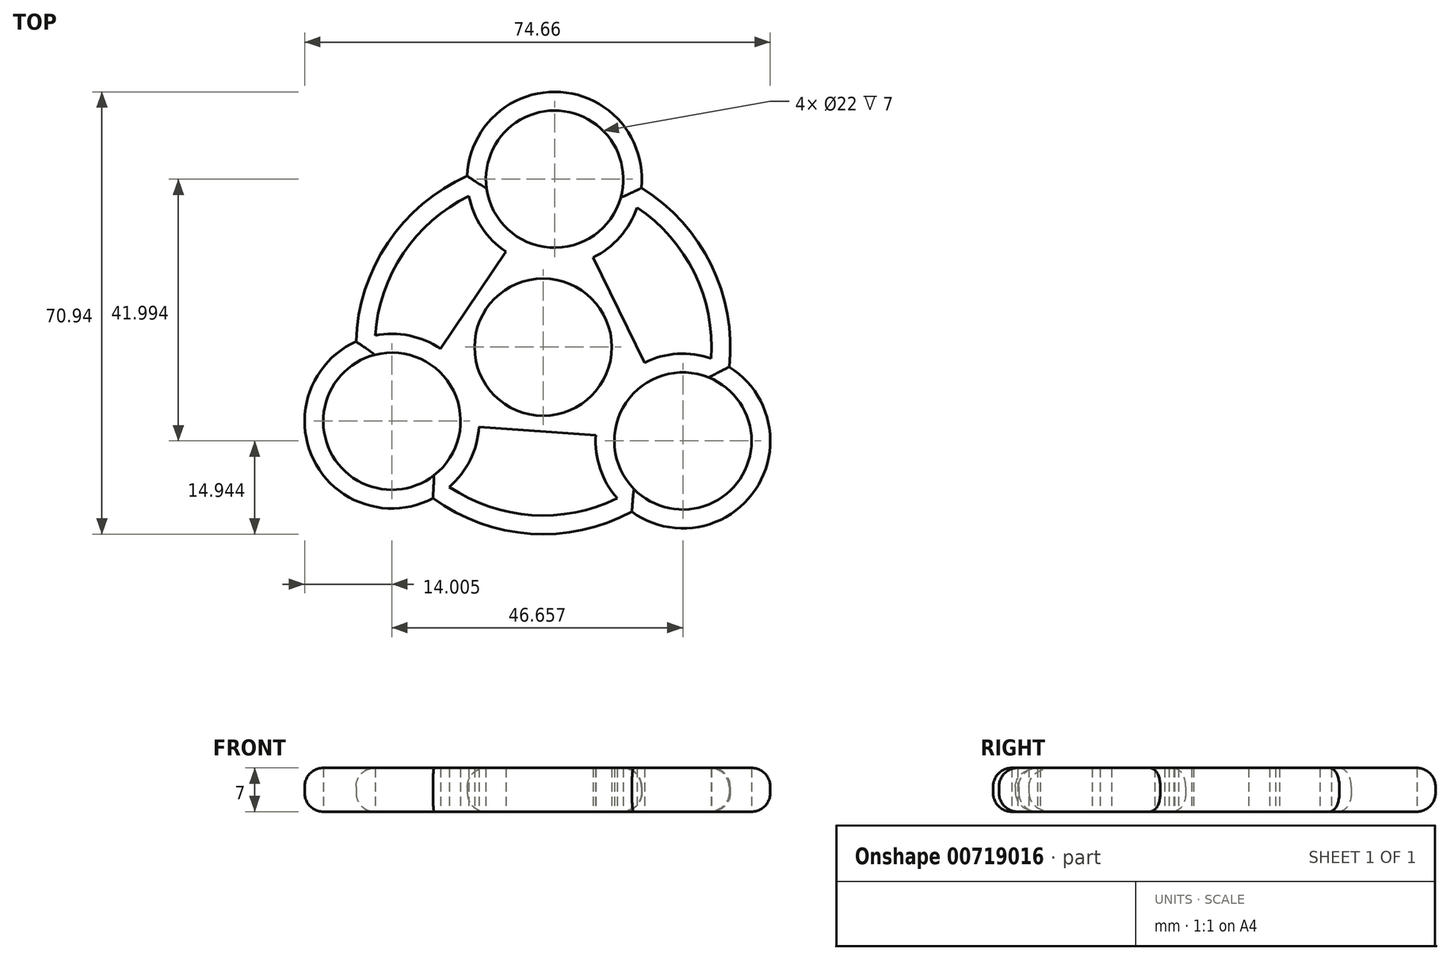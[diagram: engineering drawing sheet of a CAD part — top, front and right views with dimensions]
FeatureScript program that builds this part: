
annotation { "Feature Type Name" : "Feature", "Feature Type Description" : "" }
export const myFeature = defineFeature(function(context is Context, id is Id, definition is map)
    precondition{}
    {
        {
            var Q0;
            Q0=qCreatedBy(makeId("Top.planeOp"),FACE);
            var sketch = newSketch(context, id + "F0", { "sketchPlane" : qUnion([Q0])});
            skCircle(sketch, "E0", {"center": v(0, 0) * mm, "radius": 11 * mm});
            skCircle(sketch, "E1.cCircle", {"center": v(0, 0) * mm, "radius": 27 * mm, "construction": true});
            skLineSegment(sketch, "E1.0", {"start": v(22.41, -15.06) * mm, "end": v(-24.25, -11.88) * mm});
            skLineSegment(sketch, "E1.1", {"start": v(-24.25, -11.88) * mm, "end": v(1.83, 26.94) * mm});
            skLineSegment(sketch, "E1.2", {"start": v(1.83, 26.94) * mm, "end": v(22.41, -15.06) * mm});
            skCircle(sketch, "E2", {"center": v(-24.25, -11.88) * mm, "radius": 11 * mm});
            skCircle(sketch, "E3", {"center": v(1.83, 26.94) * mm, "radius": 11 * mm});
            skCircle(sketch, "E4", {"center": v(22.41, -15.06) * mm, "radius": 11 * mm});
            skCircle(sketch, "E5", {"center": v(-24.25, -11.88) * mm, "radius": 14 * mm});
            skCircle(sketch, "E6", {"center": v(22.41, -15.06) * mm, "radius": 14 * mm});
            skCircle(sketch, "E7", {"center": v(0, 0) * mm, "radius": 15 * mm});
            skCircle(sketch, "E8", {"center": v(1.83, 26.94) * mm, "radius": 14 * mm});
            skCircle(sketch, "E9", {"center": v(0, 0) * mm, "radius": 30 * mm});
            skCircle(sketch, "E10", {"center": v(0, 0) * mm, "radius": 27 * mm});
            skSolve(sketch);
        }
        {
            var Q0;
            {var subQ0=sQuery(id+"F0.wireOp",EDGE,"E9");var subQ1=sQuery(id+"F0.wireOp",EDGE,"E5");var subQ2=makeQuery(id+"F0.imprint","INTERSECT",VERTEX,{"disambiguationData":[OD(1.0)],"derivedFrom":[subQ1,subQ0]});Q0=makeQuery(id+"F0.imprint","IMPRINT",FACE,{"disambiguationData":[TD([[makeQuery(id+"F0.imprint","IMPRINT",EDGE,{"disambiguationData":[TD([[subQ2,-1.0]])],"derivedFrom":subQ1}),-1.0]])]});}
            var Q1;
            {var subQ0=sQuery(id+"F0.wireOp",EDGE,"E9");var subQ1=sQuery(id+"F0.wireOp",EDGE,"E4");var subQ2=makeQuery(id+"F0.imprint","INTERSECT",VERTEX,{"disambiguationData":[OD(0.0)],"derivedFrom":[subQ1,subQ0]});Q1=makeQuery(id+"F0.imprint","IMPRINT",FACE,{"disambiguationData":[TD([[makeQuery(id+"F0.imprint","IMPRINT",EDGE,{"disambiguationData":[TD([[subQ2,1.0]])],"derivedFrom":subQ1}),-1.0]])]});}
            var Q2;
            {var subQ0=sQuery(id+"F0.wireOp",EDGE,"E10");var subQ1=sQuery(id+"F0.wireOp",EDGE,"E4");var subQ2=makeQuery(id+"F0.imprint","INTERSECT",VERTEX,{"disambiguationData":[OD(1.0)],"derivedFrom":[subQ1,subQ0]});Q2=makeQuery(id+"F0.imprint","IMPRINT",FACE,{"disambiguationData":[TD([[makeQuery(id+"F0.imprint","IMPRINT",EDGE,{"disambiguationData":[TD([[subQ2,-1.0]])],"derivedFrom":subQ1}),-1.0]])]});}
            var Q3;
            {var subQ0=sQuery(id+"F0.wireOp",EDGE,"E4");var subQ1=sQuery(id+"F0.wireOp",EDGE,"E1.0");var subQ2=makeQuery(id+"F0.imprint","INTERSECT",VERTEX,{"derivedFrom":[subQ1,subQ0]});Q3=makeQuery(id+"F0.imprint","IMPRINT",FACE,{"disambiguationData":[TD([[makeQuery(id+"F0.imprint","IMPRINT",EDGE,{"disambiguationData":[TD([[subQ2,-1.0]])],"derivedFrom":subQ1}),1.0]])]});}
            var Q4;
            {var subQ0=sQuery(id+"F0.wireOp",EDGE,"E10");var subQ1=sQuery(id+"F0.wireOp",EDGE,"E4");var subQ2=makeQuery(id+"F0.imprint","INTERSECT",VERTEX,{"disambiguationData":[OD(0.0)],"derivedFrom":[subQ1,subQ0]});Q4=makeQuery(id+"F0.imprint","IMPRINT",FACE,{"disambiguationData":[TD([[makeQuery(id+"F0.imprint","IMPRINT",EDGE,{"disambiguationData":[TD([[subQ2,1.0]])],"derivedFrom":subQ1}),-1.0]])]});}
            var Q5;
            {var subQ0=sQuery(id+"F0.wireOp",EDGE,"E9");var subQ1=sQuery(id+"F0.wireOp",EDGE,"E6");var subQ2=makeQuery(id+"F0.imprint","INTERSECT",VERTEX,{"disambiguationData":[OD(0.0)],"derivedFrom":[subQ1,subQ0]});Q5=makeQuery(id+"F0.imprint","IMPRINT",FACE,{"disambiguationData":[TD([[makeQuery(id+"F0.imprint","IMPRINT",EDGE,{"disambiguationData":[TD([[subQ2,-1.0]])],"derivedFrom":subQ1}),-1.0]])]});}
            var Q6;
            {var subQ0=sQuery(id+"F0.wireOp",EDGE,"E9");var subQ1=sQuery(id+"F0.wireOp",EDGE,"E3");var subQ2=makeQuery(id+"F0.imprint","INTERSECT",VERTEX,{"disambiguationData":[OD(0.0)],"derivedFrom":[subQ1,subQ0]});Q6=makeQuery(id+"F0.imprint","IMPRINT",FACE,{"disambiguationData":[TD([[makeQuery(id+"F0.imprint","IMPRINT",EDGE,{"disambiguationData":[TD([[subQ2,1.0]])],"derivedFrom":subQ1}),-1.0]])]});}
            var Q7;
            {var subQ0=sQuery(id+"F0.wireOp",EDGE,"E9");var subQ1=sQuery(id+"F0.wireOp",EDGE,"E2");var subQ2=makeQuery(id+"F0.imprint","INTERSECT",VERTEX,{"disambiguationData":[OD(0.0)],"derivedFrom":[subQ1,subQ0]});Q7=makeQuery(id+"F0.imprint","IMPRINT",FACE,{"disambiguationData":[TD([[makeQuery(id+"F0.imprint","IMPRINT",EDGE,{"disambiguationData":[TD([[subQ2,-1.0]])],"derivedFrom":subQ1}),-1.0]])]});}
            var Q8;
            {var subQ0=sQuery(id+"F0.wireOp",EDGE,"E9");var subQ1=sQuery(id+"F0.wireOp",EDGE,"E2");var subQ2=makeQuery(id+"F0.imprint","INTERSECT",VERTEX,{"disambiguationData":[OD(1.0)],"derivedFrom":[subQ1,subQ0]});Q8=makeQuery(id+"F0.imprint","IMPRINT",FACE,{"disambiguationData":[TD([[makeQuery(id+"F0.imprint","IMPRINT",EDGE,{"disambiguationData":[TD([[subQ2,-1.0]])],"derivedFrom":subQ1}),-1.0]])]});}
            var Q9;
            {var subQ0=sQuery(id+"F0.wireOp",EDGE,"E9");var subQ1=sQuery(id+"F0.wireOp",EDGE,"E5");var subQ2=makeQuery(id+"F0.imprint","INTERSECT",VERTEX,{"disambiguationData":[OD(0.0)],"derivedFrom":[subQ1,subQ0]});Q9=makeQuery(id+"F0.imprint","IMPRINT",FACE,{"disambiguationData":[TD([[makeQuery(id+"F0.imprint","IMPRINT",EDGE,{"disambiguationData":[TD([[subQ2,1.0]])],"derivedFrom":subQ1}),-1.0]])]});}
            var Q10;
            {var subQ0=sQuery(id+"F0.wireOp",EDGE,"E10");var subQ1=sQuery(id+"F0.wireOp",EDGE,"E2");var subQ2=makeQuery(id+"F0.imprint","INTERSECT",VERTEX,{"disambiguationData":[OD(0.0)],"derivedFrom":[subQ1,subQ0]});Q10=makeQuery(id+"F0.imprint","IMPRINT",FACE,{"disambiguationData":[TD([[makeQuery(id+"F0.imprint","IMPRINT",EDGE,{"disambiguationData":[TD([[subQ2,-1.0]])],"derivedFrom":subQ1}),-1.0]])]});}
            var Q11;
            {var subQ0=sQuery(id+"F0.wireOp",EDGE,"E5");var subQ1=sQuery(id+"F0.wireOp",EDGE,"E1.0");var subQ2=makeQuery(id+"F0.imprint","INTERSECT",VERTEX,{"derivedFrom":[subQ1,subQ0]});Q11=makeQuery(id+"F0.imprint","IMPRINT",FACE,{"disambiguationData":[TD([[makeQuery(id+"F0.imprint","IMPRINT",EDGE,{"disambiguationData":[TD([[subQ2,-1.0]])],"derivedFrom":subQ1}),1.0]])]});}
            var Q12;
            {var subQ0=sQuery(id+"F0.wireOp",EDGE,"E2");var subQ1=sQuery(id+"F0.wireOp",EDGE,"E1.1");var subQ2=makeQuery(id+"F0.imprint","INTERSECT",VERTEX,{"derivedFrom":[subQ1,subQ0]});Q12=makeQuery(id+"F0.imprint","IMPRINT",FACE,{"disambiguationData":[TD([[makeQuery(id+"F0.imprint","IMPRINT",EDGE,{"disambiguationData":[TD([[subQ2,-1.0]])],"derivedFrom":subQ1}),1.0]])]});}
            var Q13;
            {var subQ0=sQuery(id+"F0.wireOp",EDGE,"E3");var subQ1=sQuery(id+"F0.wireOp",EDGE,"E1.2");var subQ2=makeQuery(id+"F0.imprint","INTERSECT",VERTEX,{"derivedFrom":[subQ1,subQ0]});Q13=makeQuery(id+"F0.imprint","IMPRINT",FACE,{"disambiguationData":[TD([[makeQuery(id+"F0.imprint","IMPRINT",EDGE,{"disambiguationData":[TD([[subQ2,-1.0]])],"derivedFrom":subQ1}),1.0]])]});}
            var Q14;
            {var subQ0=sQuery(id+"F0.wireOp",EDGE,"E6");var subQ1=sQuery(id+"F0.wireOp",EDGE,"E1.2");var subQ2=makeQuery(id+"F0.imprint","INTERSECT",VERTEX,{"derivedFrom":[subQ1,subQ0]});Q14=makeQuery(id+"F0.imprint","IMPRINT",FACE,{"disambiguationData":[TD([[makeQuery(id+"F0.imprint","IMPRINT",EDGE,{"disambiguationData":[TD([[subQ2,-1.0]])],"derivedFrom":subQ1}),1.0]])]});}
            var Q15;
            {var subQ0=sQuery(id+"F0.wireOp",EDGE,"E9");var subQ1=sQuery(id+"F0.wireOp",EDGE,"E3");var subQ2=makeQuery(id+"F0.imprint","INTERSECT",VERTEX,{"disambiguationData":[OD(1.0)],"derivedFrom":[subQ1,subQ0]});Q15=makeQuery(id+"F0.imprint","IMPRINT",FACE,{"disambiguationData":[TD([[makeQuery(id+"F0.imprint","IMPRINT",EDGE,{"disambiguationData":[TD([[subQ2,1.0]])],"derivedFrom":subQ1}),-1.0]])]});}
            var Q16;
            {var subQ0=sQuery(id+"F0.wireOp",EDGE,"E9");var subQ1=sQuery(id+"F0.wireOp",EDGE,"E3");var subQ2=makeQuery(id+"F0.imprint","INTERSECT",VERTEX,{"disambiguationData":[OD(0.0)],"derivedFrom":[subQ1,subQ0]});Q16=makeQuery(id+"F0.imprint","IMPRINT",FACE,{"disambiguationData":[TD([[makeQuery(id+"F0.imprint","IMPRINT",EDGE,{"disambiguationData":[TD([[subQ2,-1.0]])],"derivedFrom":subQ1}),-1.0]])]});}
            var Q17;
            {var subQ0=sQuery(id+"F0.wireOp",EDGE,"E8");var subQ1=sQuery(id+"F0.wireOp",EDGE,"E1.1");var subQ2=makeQuery(id+"F0.imprint","INTERSECT",VERTEX,{"derivedFrom":[subQ1,subQ0]});Q17=makeQuery(id+"F0.imprint","IMPRINT",FACE,{"disambiguationData":[TD([[makeQuery(id+"F0.imprint","IMPRINT",EDGE,{"disambiguationData":[TD([[subQ2,-1.0]])],"derivedFrom":subQ1}),1.0]])]});}
            var Q18;
            {var subQ0=sQuery(id+"F0.wireOp",EDGE,"E4");var subQ1=sQuery(id+"F0.wireOp",EDGE,"E1.0");var subQ2=makeQuery(id+"F0.imprint","INTERSECT",VERTEX,{"derivedFrom":[subQ1,subQ0]});Q18=makeQuery(id+"F0.imprint","IMPRINT",FACE,{"disambiguationData":[TD([[makeQuery(id+"F0.imprint","IMPRINT",EDGE,{"disambiguationData":[TD([[subQ2,-1.0]])],"derivedFrom":subQ1}),-1.0]])]});}
            var Q19;
            {var subQ1=sQuery(id+"F0.wireOp",EDGE,"E1.0");var subQ5=sQuery(id+"F0.wireOp",EDGE,"E5");var subQ9=makeQuery(id+"F0.imprint","INTERSECT",VERTEX,{"derivedFrom":[subQ1,subQ5]});Q19=makeQuery(id+"F0.imprint","IMPRINT",FACE,{"disambiguationData":[TD([[makeQuery(id+"F0.imprint","IMPRINT",EDGE,{"disambiguationData":[TD([[subQ9,-1.0]])],"derivedFrom":subQ1}),-1.0]])]});}
            var Q20;
            {var subQ1=sQuery(id+"F0.wireOp",EDGE,"E1.1");var subQ5=sQuery(id+"F0.wireOp",EDGE,"E8");var subQ10=makeQuery(id+"F0.imprint","INTERSECT",VERTEX,{"derivedFrom":[subQ1,subQ5]});Q20=makeQuery(id+"F0.imprint","IMPRINT",FACE,{"disambiguationData":[TD([[makeQuery(id+"F0.imprint","IMPRINT",EDGE,{"disambiguationData":[TD([[subQ10,-1.0]])],"derivedFrom":subQ1}),-1.0]])]});}
            var Q21;
            {var subQ0=sQuery(id+"F0.wireOp",EDGE,"E7");var subQ1=sQuery(id+"F0.wireOp",EDGE,"E1.2");var subQ2=makeQuery(id+"F0.imprint","INTERSECT",VERTEX,{"disambiguationData":[OD(1.0)],"derivedFrom":[subQ1,subQ0]});Q21=makeQuery(id+"F0.imprint","IMPRINT",FACE,{"disambiguationData":[TD([[makeQuery(id+"F0.imprint","IMPRINT",EDGE,{"disambiguationData":[TD([[subQ2,-1.0]])],"derivedFrom":subQ1}),-1.0]])]});}
            var Q22;
            {var subQ0=sQuery(id+"F0.wireOp",EDGE,"E6");var subQ1=sQuery(id+"F0.wireOp",EDGE,"E1.0");var subQ2=makeQuery(id+"F0.imprint","INTERSECT",VERTEX,{"derivedFrom":[subQ1,subQ0]});Q22=makeQuery(id+"F0.imprint","IMPRINT",FACE,{"disambiguationData":[TD([[makeQuery(id+"F0.imprint","IMPRINT",EDGE,{"disambiguationData":[TD([[subQ2,-1.0]])],"derivedFrom":subQ1}),-1.0]])]});}
            var Q23;
            {var subQ0=sQuery(id+"F0.wireOp",EDGE,"E7");var subQ1=sQuery(id+"F0.wireOp",EDGE,"E1.0");var subQ2=makeQuery(id+"F0.imprint","INTERSECT",VERTEX,{"disambiguationData":[OD(1.0)],"derivedFrom":[subQ1,subQ0]});Q23=makeQuery(id+"F0.imprint","IMPRINT",FACE,{"disambiguationData":[TD([[makeQuery(id+"F0.imprint","IMPRINT",EDGE,{"disambiguationData":[TD([[subQ2,-1.0]])],"derivedFrom":subQ1}),-1.0]])]});}
            var Q24;
            {var subQ0=sQuery(id+"F0.wireOp",EDGE,"E5");var subQ1=sQuery(id+"F0.wireOp",EDGE,"E1.1");var subQ2=makeQuery(id+"F0.imprint","INTERSECT",VERTEX,{"derivedFrom":[subQ1,subQ0]});Q24=makeQuery(id+"F0.imprint","IMPRINT",FACE,{"disambiguationData":[TD([[makeQuery(id+"F0.imprint","IMPRINT",EDGE,{"disambiguationData":[TD([[subQ2,-1.0]])],"derivedFrom":subQ1}),-1.0]])]});}
            var Q25;
            {var subQ0=sQuery(id+"F0.wireOp",EDGE,"E7");var subQ1=sQuery(id+"F0.wireOp",EDGE,"E1.1");var subQ2=makeQuery(id+"F0.imprint","INTERSECT",VERTEX,{"disambiguationData":[OD(1.0)],"derivedFrom":[subQ1,subQ0]});Q25=makeQuery(id+"F0.imprint","IMPRINT",FACE,{"disambiguationData":[TD([[makeQuery(id+"F0.imprint","IMPRINT",EDGE,{"disambiguationData":[TD([[subQ2,-1.0]])],"derivedFrom":subQ1}),-1.0]])]});}
            var Q26;
            {var subQ0=sQuery(id+"F0.wireOp",EDGE,"E8");var subQ1=sQuery(id+"F0.wireOp",EDGE,"E1.2");var subQ2=makeQuery(id+"F0.imprint","INTERSECT",VERTEX,{"derivedFrom":[subQ1,subQ0]});Q26=makeQuery(id+"F0.imprint","IMPRINT",FACE,{"disambiguationData":[TD([[makeQuery(id+"F0.imprint","IMPRINT",EDGE,{"disambiguationData":[TD([[subQ2,-1.0]])],"derivedFrom":subQ1}),-1.0]])]});}
            var Q27;
            Q27=makeQuery(id+"F0.imprint","IMPRINT",FACE,{"disambiguationData":[TD([[makeQuery(id+"F0.imprint","IMPRINT",EDGE,{"derivedFrom":sQuery(id+"F0.wireOp",EDGE,"E0")}),-1.0]])]});
            var Q28;
            {var subQ0=sQuery(id+"F0.wireOp",EDGE,"E7");var subQ1=sQuery(id+"F0.wireOp",EDGE,"E5");var subQ2=makeQuery(id+"F0.imprint","INTERSECT",VERTEX,{"disambiguationData":[OD(0.0)],"derivedFrom":[subQ1,subQ0]});Q28=makeQuery(id+"F0.imprint","IMPRINT",FACE,{"disambiguationData":[TD([[makeQuery(id+"F0.imprint","IMPRINT",EDGE,{"disambiguationData":[TD([[subQ2,1.0]])],"derivedFrom":subQ1}),1.0]])]});}
            var Q29;
            {var subQ0=sQuery(id+"F0.wireOp",EDGE,"E8");var subQ1=sQuery(id+"F0.wireOp",EDGE,"E7");var subQ2=makeQuery(id+"F0.imprint","INTERSECT",VERTEX,{"disambiguationData":[OD(0.0)],"derivedFrom":[subQ1,subQ0]});Q29=makeQuery(id+"F0.imprint","IMPRINT",FACE,{"disambiguationData":[TD([[makeQuery(id+"F0.imprint","IMPRINT",EDGE,{"disambiguationData":[TD([[subQ2,-1.0]])],"derivedFrom":subQ1}),1.0]])]});}
            var Q30;
            {var subQ0=sQuery(id+"F0.wireOp",EDGE,"E7");var subQ1=sQuery(id+"F0.wireOp",EDGE,"E6");var subQ2=makeQuery(id+"F0.imprint","INTERSECT",VERTEX,{"disambiguationData":[OD(0.0)],"derivedFrom":[subQ1,subQ0]});Q30=makeQuery(id+"F0.imprint","IMPRINT",FACE,{"disambiguationData":[TD([[makeQuery(id+"F0.imprint","IMPRINT",EDGE,{"disambiguationData":[TD([[subQ2,-1.0]])],"derivedFrom":subQ1}),1.0]])]});}
            extrude(context, id + "F1", {"entities" : qUnion([Q0, Q1, Q2, Q3, Q4, Q5, Q6, Q7, Q8, Q9, Q10, Q11, Q12, Q13, Q14, Q15, Q16, Q17, Q18, Q19, Q20, Q21, Q22, Q23, Q24, Q25, Q26, Q27, Q28, Q29, Q30]), "depth" : 7 * mm, "offsetDistance" : 25 * mm});
        }
        {
            var Q0;
            {var subQ0=sQuery(id+"F0.wireOp",EDGE,"E9");Q0=makeQuery(id+"F1.opExtrude","CAP_EDGE",EDGE,{"disambiguationData":[OSD([subQ0]),TDD([makeQuery(id+"F0.imprint","IMPRINT",EDGE,{"disambiguationData":[TD([[makeQuery(id+"F0.imprint","INTERSECT",VERTEX,{"disambiguationData":[OD(1.0)],"derivedFrom":[sQuery(id+"F0.wireOp",EDGE,"E5"),subQ0]}),-1.0]])],"derivedFrom":subQ0})])],"isStart":false});}
            var Q1;
            {var subQ0=sQuery(id+"F0.wireOp",EDGE,"E9");var subQ1=sQuery(id+"F0.wireOp",EDGE,"E6");Q1=makeQuery(id+"F1.opExtrude","CAP_EDGE",EDGE,{"disambiguationData":[OSD([subQ1]),TDD([makeQuery(id+"F0.imprint","IMPRINT",EDGE,{"disambiguationData":[TD([[makeQuery(id+"F0.imprint","INTERSECT",VERTEX,{"disambiguationData":[OD(0.0)],"derivedFrom":[subQ1,subQ0]}),1.0]])],"derivedFrom":subQ1})])],"isStart":false});}
            var Q2;
            {var subQ0=sQuery(id+"F0.wireOp",EDGE,"E9");var subQ1=sQuery(id+"F0.wireOp",EDGE,"E8");Q2=makeQuery(id+"F1.opExtrude","CAP_EDGE",EDGE,{"disambiguationData":[OSD([subQ1]),TDD([makeQuery(id+"F0.imprint","IMPRINT",EDGE,{"disambiguationData":[TD([[makeQuery(id+"F0.imprint","INTERSECT",VERTEX,{"disambiguationData":[OD(0.0)],"derivedFrom":[subQ1,subQ0]}),1.0]])],"derivedFrom":subQ1})])],"isStart":false});}
            var Q3;
            {var subQ0=sQuery(id+"F0.wireOp",EDGE,"E9");Q3=makeQuery(id+"F1.opExtrude","CAP_EDGE",EDGE,{"disambiguationData":[OSD([subQ0]),TDD([makeQuery(id+"F0.imprint","IMPRINT",EDGE,{"disambiguationData":[TD([[makeQuery(id+"F0.imprint","INTERSECT",VERTEX,{"disambiguationData":[OD(0.0)],"derivedFrom":[sQuery(id+"F0.wireOp",EDGE,"E5"),subQ0]}),1.0]])],"derivedFrom":subQ0})])],"isStart":false});}
            var Q4;
            {var subQ0=sQuery(id+"F0.wireOp",EDGE,"E9");var subQ1=sQuery(id+"F0.wireOp",EDGE,"E5");Q4=makeQuery(id+"F1.opExtrude","CAP_EDGE",EDGE,{"disambiguationData":[OSD([subQ1]),TDD([makeQuery(id+"F0.imprint","IMPRINT",EDGE,{"disambiguationData":[TD([[makeQuery(id+"F0.imprint","INTERSECT",VERTEX,{"disambiguationData":[OD(0.0)],"derivedFrom":[subQ1,subQ0]}),-1.0]])],"derivedFrom":subQ1})])],"isStart":false});}
            var Q5;
            {var subQ0=sQuery(id+"F0.wireOp",EDGE,"E9");var subQ1=sQuery(id+"F0.wireOp",EDGE,"E8");Q5=makeQuery(id+"F1.opExtrude","CAP_EDGE",EDGE,{"disambiguationData":[OSD([subQ1]),TDD([makeQuery(id+"F0.imprint","IMPRINT",EDGE,{"disambiguationData":[TD([[makeQuery(id+"F0.imprint","INTERSECT",VERTEX,{"disambiguationData":[OD(0.0)],"derivedFrom":[subQ1,subQ0]}),1.0]])],"derivedFrom":subQ1})])],"isStart":true});}
            var Q6;
            {var subQ0=sQuery(id+"F0.wireOp",EDGE,"E9");Q6=makeQuery(id+"F1.opExtrude","CAP_EDGE",EDGE,{"disambiguationData":[OSD([subQ0]),TDD([makeQuery(id+"F0.imprint","IMPRINT",EDGE,{"disambiguationData":[TD([[makeQuery(id+"F0.imprint","INTERSECT",VERTEX,{"disambiguationData":[OD(0.0)],"derivedFrom":[sQuery(id+"F0.wireOp",EDGE,"E5"),subQ0]}),1.0]])],"derivedFrom":subQ0})])],"isStart":true});}
            var Q7;
            {var subQ0=sQuery(id+"F0.wireOp",EDGE,"E9");var subQ1=sQuery(id+"F0.wireOp",EDGE,"E6");Q7=makeQuery(id+"F1.opExtrude","CAP_EDGE",EDGE,{"disambiguationData":[OSD([subQ1]),TDD([makeQuery(id+"F0.imprint","IMPRINT",EDGE,{"disambiguationData":[TD([[makeQuery(id+"F0.imprint","INTERSECT",VERTEX,{"disambiguationData":[OD(0.0)],"derivedFrom":[subQ1,subQ0]}),1.0]])],"derivedFrom":subQ1})])],"isStart":true});}
            var Q8;
            {var subQ0=sQuery(id+"F0.wireOp",EDGE,"E9");Q8=makeQuery(id+"F1.opExtrude","CAP_EDGE",EDGE,{"disambiguationData":[OSD([subQ0]),TDD([makeQuery(id+"F0.imprint","IMPRINT",EDGE,{"disambiguationData":[TD([[makeQuery(id+"F0.imprint","INTERSECT",VERTEX,{"disambiguationData":[OD(1.0)],"derivedFrom":[sQuery(id+"F0.wireOp",EDGE,"E5"),subQ0]}),-1.0]])],"derivedFrom":subQ0})])],"isStart":true});}
            var Q9;
            {var subQ0=sQuery(id+"F0.wireOp",EDGE,"E9");var subQ1=sQuery(id+"F0.wireOp",EDGE,"E5");Q9=makeQuery(id+"F1.opExtrude","CAP_EDGE",EDGE,{"disambiguationData":[OSD([subQ1]),TDD([makeQuery(id+"F0.imprint","IMPRINT",EDGE,{"disambiguationData":[TD([[makeQuery(id+"F0.imprint","INTERSECT",VERTEX,{"disambiguationData":[OD(0.0)],"derivedFrom":[subQ1,subQ0]}),-1.0]])],"derivedFrom":subQ1})])],"isStart":true});}
            var Q10;
            {var subQ0=sQuery(id+"F0.wireOp",EDGE,"E9");Q10=makeQuery(id+"F1.opExtrude","CAP_EDGE",EDGE,{"disambiguationData":[OSD([subQ0]),TDD([makeQuery(id+"F0.imprint","IMPRINT",EDGE,{"disambiguationData":[TD([[makeQuery(id+"F0.imprint","INTERSECT",VERTEX,{"disambiguationData":[OD(0.0)],"derivedFrom":[sQuery(id+"F0.wireOp",EDGE,"E6"),subQ0]}),-1.0]])],"derivedFrom":subQ0})])],"isStart":false});}
            var Q11;
            {var subQ0=sQuery(id+"F0.wireOp",EDGE,"E9");Q11=makeQuery(id+"F1.opExtrude","CAP_EDGE",EDGE,{"disambiguationData":[OSD([subQ0]),TDD([makeQuery(id+"F0.imprint","IMPRINT",EDGE,{"disambiguationData":[TD([[makeQuery(id+"F0.imprint","INTERSECT",VERTEX,{"disambiguationData":[OD(0.0)],"derivedFrom":[sQuery(id+"F0.wireOp",EDGE,"E6"),subQ0]}),-1.0]])],"derivedFrom":subQ0})])],"isStart":true});}
            fillet(context, id + "F2", {"entities" : qUnion([Q0, Q1, Q2, Q3, Q4, Q5, Q6, Q7, Q8, Q9, Q10, Q11]), "radius" : 3 * mm, "tangentPropagation" : true, "allowEdgeOverflow" : false});
        }
    });
